# Revit family: Door-Rolling-Grille_300_BetweenJambMount_CornellIron
name_source: partatom
category: Doors
revit_build: Autodesk Revit MEP 2013 (Build: 20130531_2115(x64)
units: mm (PartAtom-declared; Revit-internal decimal feet)

## types (1)
- Motor Operated, Aluminium (Mill Finish), 9" Vertical Spacing
    # Of Straight Grills = 37
    # of Brick Grills = 37
    04 CSI = 08 33 00
    95 CSI = 08330
    Assembly Code = B2030410
    Bottom Bar = Aluminum, mill finish
    Brick Vertical Spacing = 0' - 2"
    Coil Dimension Note = 13” to 20” - Consult Cornell when dimensions are critical.
    Control Box Height = 4' - 0"
    Control Box Offset = 2' - 0"
    Curtain Brick = Yes
    Curtain Rods 2In OC Standard = Aluminum, mill finish
    Curtain Spacing Vertical Chains 3In OC = No
    Curtain Spacing Vertical Chains 6In OC = No
    Curtain Spacing Vertical Chains 9In OC = Yes
    Curtain Straight = No
    Description = Built to order, open curtain grilles provide security, visual access of separated areas.
    Distributor Locator = http://www.cornelliron.com
    From Coil Side Operate on Left = No
    From Coil Side Operate on Right = Yes
    Function = Interior
    Gard Width = 9' - 2 1/2"
    Guides = Aluminum, mill finish
    Hand Crank = No
    Height = 12' - 0"
    Hood = Aluminum, mill finish
    Hood Width = 8' - 4"
    Horizontal Spacing = 0' - 9"
    Jamb Dimension Note = 5” to 6 1/2” wide. Consult Cornell when dimensions are critical.
    Jamb Height = 14' - 4"
    Manufacturer = Cornell Iron Works
    Model = 300
    Motor Horizontal = No
    Mounting = Between Jambs
    Operator = Operator : Motor Operator
    Operator Cover Left = No
    Operator Cover Right = Yes
    Operator Height = 5' - 4"
    Optional aluminum, color anodized finish = No
    Product Options = Open Curtain Brick Pattern, Glazed Curtain, Injection molded link curtain. High Cycle Construction (>20/day)
    Representative Disclaimer = Cornell products are sold and installed through a nationwide network of independent distributors.
    Revit Object Download Link = http://cornellcookson.smartbim.com
    Rough Width = 5' - 8 1/2"
    Shutter Height = 12' - 0"
    Shutter Width = 9' - 2 1/4"
    Sizing Disclaimer = Openings up to 40’ wide x 20’ high standard construction. Consult Cornell for larger sizes.
    Subcategory = Roll Up
    URL = http://www.cornelliron.com
    URL CAD = http://pricing.cornelliron.com
    URL Photographs = http://www.cornelliron.com
    Vertical Spacing = 0' - 2"
    Wall Closure = By host
    Wall Construction = Self supporting tubes, Masonry, Steel or Wood
    Width = 10' - 0"

## geometry (parser evidence)
native form markers: Blend x14, Sweep x25
no freeform markers — native parametric forms only
